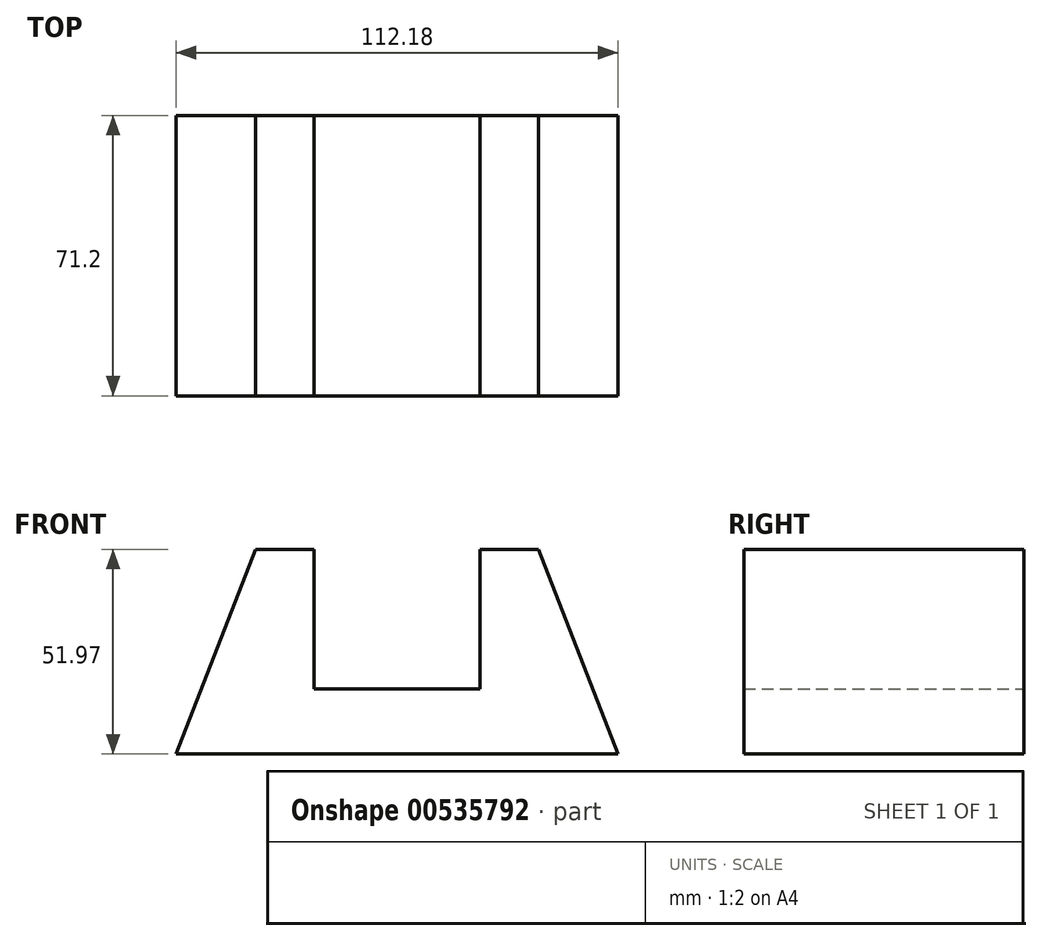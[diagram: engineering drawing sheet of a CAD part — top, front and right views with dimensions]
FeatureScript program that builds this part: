
annotation { "Feature Type Name" : "Feature", "Feature Type Description" : "" }
export const myFeature = defineFeature(function(context is Context, id is Id, definition is map)
    precondition{}
    {
        {
            var Q0;
            Q0=qCreatedBy(makeId("Front.planeOp"),FACE);
            var sketch = newSketch(context, id + "F0", { "sketchPlane" : qUnion([Q0])});
            skLineSegment(sketch, "E0", {"start": v(0, 0) * mm, "end": v(0, 56.32) * mm, "construction": true});
            skLineSegment(sketch, "E1", {"start": v(56.09, 0) * mm, "end": v(-56.09, 0) * mm});
            skLineSegment(sketch, "E2", {"start": v(-56.09, 0) * mm, "end": v(-35.94, 51.97) * mm});
            skLineSegment(sketch, "E3", {"start": v(-35.94, 51.97) * mm, "end": v(-21.06, 51.97) * mm});
            skLineSegment(sketch, "E4", {"start": v(-21.06, 51.97) * mm, "end": v(-21.06, 16.48) * mm});
            skLineSegment(sketch, "E5", {"start": v(-21.06, 16.48) * mm, "end": v(21.06, 16.48) * mm});
            skLineSegment(sketch, "E6", {"start": v(21.06, 16.48) * mm, "end": v(21.06, 51.97) * mm});
            skLineSegment(sketch, "E7", {"start": v(21.06, 51.97) * mm, "end": v(35.94, 51.97) * mm});
            skLineSegment(sketch, "E8", {"start": v(35.94, 51.97) * mm, "end": v(56.09, 0) * mm});
            skSolve(sketch);
        }
        {
            var Q0;
            Q0=makeQuery(id+"F0.imprint","IMPRINT",FACE,{"disambiguationData":[TD([[makeQuery(id+"F0.imprint","IMPRINT",EDGE,{"derivedFrom":sQuery(id+"F0.wireOp",EDGE,"E1")}),-1.0]])]});
            extrude(context, id + "F1", {"entities" : qUnion([Q0]), "endBound" : BoundingType.SYMMETRIC, "depth" : 71.2 * mm, "offsetDistance" : 25 * mm});
        }
    });
